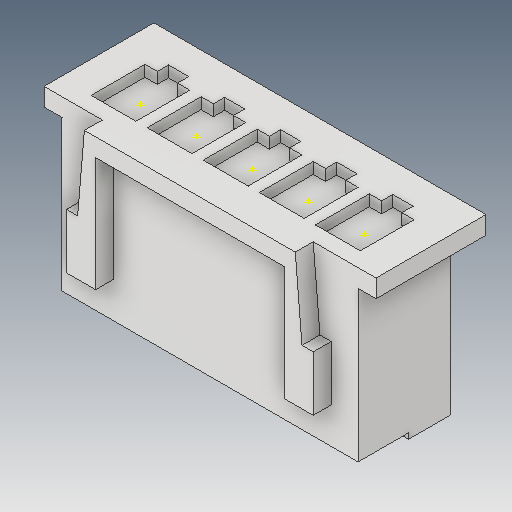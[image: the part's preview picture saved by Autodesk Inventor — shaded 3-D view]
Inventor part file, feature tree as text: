
AUTODESK INVENTOR PART (.ipt)
format: ipt  version: 2018 (Build 220112000, 112)  size: 253,952 bytes
history: native  units: mm
features: sketch x1, projected_geometry x1, other x1
ambient origin geometry x8: Origin, YZ Plane, XZ Plane, XY Plane, X Axis, Y Axis, Z Axis, Center Point
bodies: Solid1 (feature_tree)
feature tree (3):
  sketch  "Sketch1"
  projected_geometry  "Projected Loop1"
  parser-record x1  (decoder bookkeeping rows leaked as tree rows — omitted from the tree; the rows remain in map.json)
